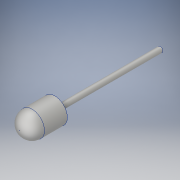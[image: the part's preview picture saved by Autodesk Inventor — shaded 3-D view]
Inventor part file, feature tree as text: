
AUTODESK INVENTOR PART (.ipt)
format: ipt  version: 2018 (Build 220112000, 112)  size: 111,616 bytes
history: native  units: in
note: dims shown in document units (in); Inventor stores cm internally (conversion verified against a paired STEP export)
features: extrude x2, sketch x2, fillet x1
ambient origin geometry x8: Origin, YZ Plane, XZ Plane, XY Plane, X Axis, Y Axis, Z Axis, Center Point
bodies: Solid1 (feature_tree)
feature tree (5):
  extrude  "Extrusion1"  Depth=1.5in TaperAngle=0.0deg
  extrude  "Extrusion2"  Depth=0.5in TaperAngle=0.0deg
  fillet  "Fillet1"  Radius=0.175in
  sketch  "Sketch1"  dims[d0=0.077in d1=1.5in d2=0.0in]
  sketch  "Sketch2"  dims[d3=0.355in d4=0.5in d5=0.0in d6=0.175in]
